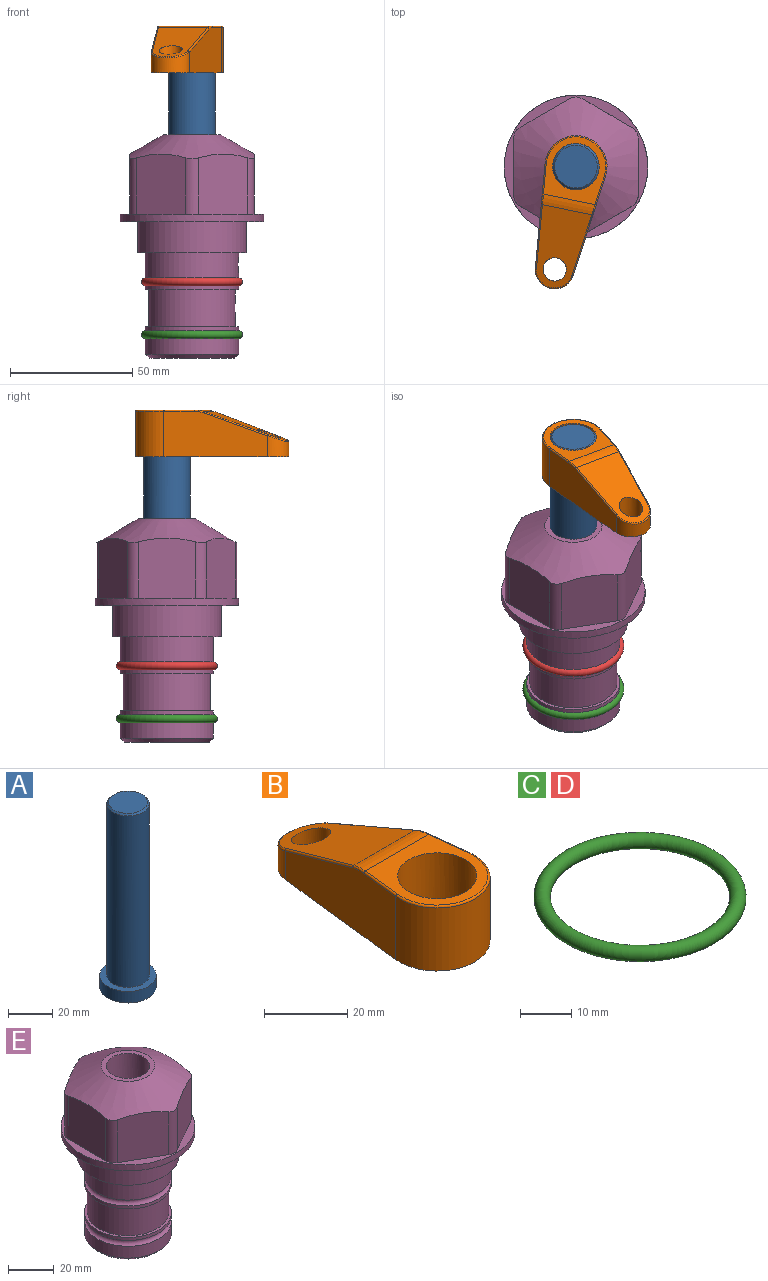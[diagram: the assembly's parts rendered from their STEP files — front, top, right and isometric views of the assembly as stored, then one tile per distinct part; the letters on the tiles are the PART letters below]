
ASSEMBLY  parts=5 mates=3
PART A: 6 faces, bbox 25.4x25.4x101.6 mm
  f0: plane 17.46x17.46mm, normal (0,0,1), area 239.5mm2, adj f5
  f1: plane 25.4x25.4mm, normal (0,0,-1), area 506.7mm2, adj f2
  f2: cylinder r=12.7mm len=25.4mm, axis (0,0,1), area 506.7mm2, adj f1,f3
  f3: plane 25.4x25.4mm, normal (0,0,1), area 221.7mm2, adj f2,f4
  f4: cylinder r=9.53mm len=94.46mm, axis (0,0,1), area 5653mm2, adj f3,f5
  f5: cone r=8.73mm half-angle=45deg, axis (0,0,-1), area 64.4mm2, adj f0,f4
PART B: 61 faces, bbox 31.5x65.5x20.3 mm
  f0: plane 16.76x11.46mm, normal (0,0,-1), area 81mm2, adj f4,f5,f6,f8,f56,f57
  f1: plane 2.3x0.95mm, normal (0,0,-1), area 1mm2, adj f26,f31,f35
  f2: plane 25.4x21.39mm, normal (0,0,-1), area 163.8mm2, adj f3,f4,f6,f7,f48,f49
  f3: cylinder r=12.7mm len=25.4mm, axis (0,0,-1), area 792.2mm2, adj f2,f4,f6,f14
  f4: plane 42.69x18.9mm, normal (0.99,0.11,0), area 647mm2, adj f0,f2,f3,f5,f12,f13,f15,f50
  f5: cylinder r=7.94mm len=15.78mm, axis (0,0,-1), area 194.3mm2, adj f0,f4,f6,f17
  f6: plane 42.69x18.9mm, normal (-0.99,0.11,0), area 647mm2, adj f0,f2,f3,f5,f16,f18,f19,f51
  f7: cylinder r=9.53mm len=19.05mm, axis (0,0,-1), area 1140.1mm2, adj f2,f9,f45,f46,f47
  f8: cylinder r=4.76mm len=10.97mm, axis (0,0,-1), area 278.8mm2, adj f0,f10,f58,f59,f60
  f9: plane 25.83x24.38mm, normal (0,0,1), area 262.2mm2, adj f7,f11,f12,f14,f16
  f10: plane 33.4x21.47mm, normal (0,0.34,0.94), area 489.9mm2, adj f8,f11,f15,f17,f19
  f11: cylinder r=12.7mm len=21.49mm, axis (-1,0,0), area 93.2mm2, adj f9,f10,f13,f18
  f12: cylinder r=0.51mm len=12.34mm, axis (0.11,-0.99,0), area 9.9mm2, adj f4,f9,f13,f14
  f13: bspline ~7.62x1.64mm, area 3.5mm2, adj f4,f11,f12,f15
  f14: torus R=12.19mm, axis (0,0,1), area 33.6mm2, adj f3,f9,f12,f16
  f15: cylinder r=0.51mm len=26.01mm, axis (0.1,-0.93,0.34), area 21.6mm2, adj f4,f10,f13,f17
  f16: cylinder r=0.51mm len=12.34mm, axis (0.11,0.99,0), area 9.9mm2, adj f6,f9,f14,f18
  f17: bspline ~15.78x7.05mm, area 15.7mm2, adj f5,f10,f15,f19
  f18: bspline ~7.62x1.64mm, area 3.5mm2, adj f6,f11,f16,f19
  f19: cylinder r=0.51mm len=26.01mm, axis (0.1,0.93,-0.34), area 21.6mm2, adj f6,f10,f17,f18
  f20: plane 21.6x9.63mm, normal (-0.99,-0.11,0), area 141.4mm2, adj f27,f29,f35,f37,f39,f52
  f21: plane 21.6x9.63mm, normal (0.99,-0.11,0), area 141.4mm2, adj f28,f30,f38,f40,f42,f53
  f22: cylinder r=12.7mm len=11.68mm, axis (0,0,-1), area 116.9mm2, adj f27,f28,f31,f32,f34,f45
  f23: cylinder r=7.94mm len=6.92mm, axis (0,0,-1), area 18.8mm2, adj f29,f30,f43,f60
  f24: plane 2.3x0.95mm, normal (0,0,-1), area 1mm2, adj f26,f34,f38
  f25: plane 17.94x12.32mm, normal (0,-0.34,-0.94), area 191.2mm2, adj f26,f39,f42,f43
  f26: cylinder r=9.53mm len=12.93mm, axis (-1,0,0), area 37.5mm2, adj f1,f24,f25,f32,f37,f40
  f27: cylinder r=1.59mm len=9.63mm, axis (0,0,-1), area 32.2mm2, adj f20,f22,f33,f46,f48,f50
  f28: cylinder r=1.59mm len=9.63mm, axis (0,0,-1), area 32.2mm2, adj f21,f22,f36,f47,f49,f51
  f29: cylinder r=1.59mm len=2.62mm, axis (0,0,-1), area 7.3mm2, adj f20,f23,f41,f54,f56,f58
  f30: cylinder r=1.59mm len=2.62mm, axis (0,0,-1), area 7.3mm2, adj f21,f23,f44,f55,f57,f59
  f31: torus R=14.29mm, axis (0,0,1), area 5.8mm2, adj f1,f22,f32,f33
  f32: bspline ~11.06x2.73mm, area 20.8mm2, adj f22,f26,f31,f34
  f33: sphere r=1.59mm, area 5.4mm2, adj f27,f31,f35
  f34: torus R=14.29mm, axis (0,0,1), area 5.8mm2, adj f22,f24,f32,f36
  f35: cylinder r=1.59mm len=1.68mm, axis (-0.11,0.99,0), area 2.4mm2, adj f1,f20,f33,f37
  f36: sphere r=1.59mm, area 5.4mm2, adj f28,f34,f38
  f37: bspline ~5.82x2.33mm, area 7.7mm2, adj f20,f26,f35,f39
  f38: cylinder r=1.59mm len=1.68mm, axis (0.11,0.99,0), area 2.4mm2, adj f21,f24,f36,f40
  f39: cylinder r=1.59mm len=18.33mm, axis (0.1,-0.93,0.34), area 46.7mm2, adj f20,f25,f37,f41
  f40: bspline ~5.82x2.33mm, area 7.7mm2, adj f21,f26,f38,f42
  f41: sphere r=1.59mm, area 3.3mm2, adj f29,f39,f43
  f42: cylinder r=1.59mm len=18.33mm, axis (0.1,0.93,-0.34), area 46.7mm2, adj f21,f25,f40,f44
  f43: bspline ~8.31x1.84mm, area 15.3mm2, adj f23,f25,f41,f44
  f44: sphere r=1.59mm, area 3.3mm2, adj f30,f42,f43
  f45: torus R=7.7mm, axis (0,0,-1), area 66.3mm2, adj f7,f22,f46,f47
  f46: bspline ~5.14x5mm, area 11.2mm2, adj f7,f27,f45,f48
  f47: bspline ~5.14x5mm, area 11.2mm2, adj f7,f28,f45,f49
  f48: torus R=6.59mm, axis (0,0,1), area 21.7mm2, adj f2,f27,f46,f50
  f49: torus R=6.59mm, axis (0,0,1), area 21.7mm2, adj f2,f28,f47,f51
  f50: bspline ~5.75x5.15mm, area 14.7mm2, adj f4,f27,f48,f52
  f51: bspline ~5x4.52mm, area 14.7mm2, adj f6,f28,f49,f53
  f52: cylinder r=5mm len=21.96mm, axis (-0.11,0.99,0), area 130.1mm2, adj f4,f20,f50,f54
  f53: cylinder r=5mm len=21.96mm, axis (-0.11,-0.99,0), area 130.1mm2, adj f6,f21,f51,f55
  f54: bspline ~6.16x5.12mm, area 14.7mm2, adj f4,f29,f52,f56
  f55: bspline ~5x4.88mm, area 14.7mm2, adj f6,f30,f53,f57
  f56: torus R=6.59mm, axis (0,0,1), area 17.9mm2, adj f0,f29,f54,f58
  f57: torus R=6.59mm, axis (0,0,1), area 17.9mm2, adj f0,f30,f55,f59
  f58: bspline ~5.16x5mm, area 9.1mm2, adj f8,f29,f56,f60
  f59: bspline ~5.16x5mm, area 9.1mm2, adj f8,f30,f57,f60
  f60: torus R=2.94mm, axis (0,0,-1), area 36.9mm2, adj f8,f23,f58,f59
PART C: 1 faces, bbox 44.7x44.7x3.2 mm
  f0: torus R=19.05mm, axis (0,0,1), area 1193.9mm2
PART D: same geometry as C
PART E: 36 faces, bbox 58.7x58.7x91.2 mm
  f0: cylinder r=17.78mm len=35.56mm, axis (0,0,1), area 1670.8mm2, adj f23,f24,f31
  f1: cylinder r=19.05mm len=38.1mm, axis (0,0,1), area 1191.9mm2, adj f26,f27,f30
  f2: plane 58.66x58.66mm, normal (0,0,-1), area 1150.6mm2, adj f3,f28
  f3: cylinder r=29.33mm len=58.66mm, axis (0,0,-1), area 585.1mm2, adj f2,f4
  f4: plane 58.66x58.66mm, normal (0,0,1), area 475.9mm2, adj f3,f5,f6,f7,f8,f9,f10,f11
  f5: plane 24.5x20.32mm, normal (-0.5,0.87,0), area 562.8mm2, adj f4,f15,f16,f17
  f6: plane 24.5x20.32mm, normal (0.5,0.87,0), area 562.8mm2, adj f4,f14,f15,f17
  f7: plane 24.5x23.48mm, normal (1,0,0), area 562.8mm2, adj f4,f13,f14,f17
  f8: plane 24.5x20.32mm, normal (0.5,-0.87,0), area 562.8mm2, adj f4,f12,f13,f17
  f9: plane 24.5x20.32mm, normal (-0.5,-0.87,0), area 562.8mm2, adj f4,f11,f12,f17
  f10: plane 24.5x23.48mm, normal (-1,0,0), area 562.8mm2, adj f4,f11,f16,f17
  f11: cylinder r=5.08mm len=23.01mm, axis (0,0,-1), area 121.2mm2, adj f4,f9,f10,f17
  f12: cylinder r=5.08mm len=23.01mm, axis (0,0,-1), area 121.2mm2, adj f4,f8,f9,f17
  f13: cylinder r=5.08mm len=23.01mm, axis (0,0,-1), area 121.2mm2, adj f4,f7,f8,f17
  f14: cylinder r=5.08mm len=23.01mm, axis (0,0,-1), area 121.2mm2, adj f4,f6,f7,f17
  f15: cylinder r=5.08mm len=23.01mm, axis (0,0,-1), area 121.2mm2, adj f4,f5,f6,f17
  f16: cylinder r=5.08mm len=23.01mm, axis (0,0,-1), area 121.2mm2, adj f4,f5,f10,f17
  f17: cone r=11.73mm half-angle=60deg, axis (0,0,-1), area 2071.8mm2, adj f5,f6,f7,f8,f9,f10,f11,f12
  f18: plane 23.46x23.46mm, normal (0,0,1), area 147.4mm2, adj f17,f35
  f19: plane 34.93x34.93mm, normal (0,0,-1), area 958mm2, adj f29
  f20: cylinder r=19.05mm len=38.1mm, axis (0,0,1), area 760.1mm2, adj f21,f29
  f21: torus R=19.05mm, axis (0,0,1), area 565.3mm2, adj f20,f22
  f22: cylinder r=19.05mm len=38.1mm, axis (0,0,1), area 190mm2, adj f21,f23
  f23: plane 38.1x38.1mm, normal (0,0,1), area 146.9mm2, adj f0,f22
  f24: plane 38.1x38.1mm, normal (0,0,-1), area 146.9mm2, adj f0,f25
  f25: cylinder r=19.05mm len=38.1mm, axis (0,0,1), area 190mm2, adj f24,f26
  f26: torus R=19.05mm, axis (0,0,1), area 565.3mm2, adj f1,f25
  f27: plane 44.45x44.45mm, normal (0,0,-1), area 411.7mm2, adj f1,f28
  f28: cylinder r=22.23mm len=44.45mm, axis (0,0,1), area 1773.5mm2, adj f2,f27
  f29: cone r=19.05mm half-angle=45deg, axis (0,0,1), area 257.5mm2, adj f19,f20
  f30: cylinder r=3.17mm len=6.75mm, axis (-1,0,0), area 128mm2, adj f1,f33
  f31: cylinder r=3.17mm len=6.35mm, axis (-1,0,0), area 102.5mm2, adj f0,f33
  f32: plane 25.4x25.4mm, normal (0,0,1), area 506.7mm2, adj f33
  f33: cylinder r=12.7mm len=66.42mm, axis (0,0,-1), area 5236.2mm2, adj f30,f31,f32,f34
  f34: cone r=9.53mm half-angle=30deg, axis (0,0,-1), area 443.4mm2, adj f33,f35
  f35: cylinder r=9.53mm len=19.05mm, axis (0,0,-1), area 849mm2, adj f18,f34
PLACE A rot(axis=(0,0,-1),101.7deg) t=(0,0,6.38)mm
PLACE B rot(axis=(0,0,1),168.3deg) t=(0,0,60.99)mm
PLACE C t=(0,0,-21.59)mm
PLACE D at identity
PLACE E at identity fixed
MATE fastened C.f0 <-> E.f0  axis (0,0,1) through (0,0,-46.1)mm
MATE cylindrical A.f2 <-> E.f0  axis (0,0,1) through (0,0,32.01)mm
MATE fastened B.f3 <-> A.f2  axis (0,0,1) through (0,0,80.04)mm
